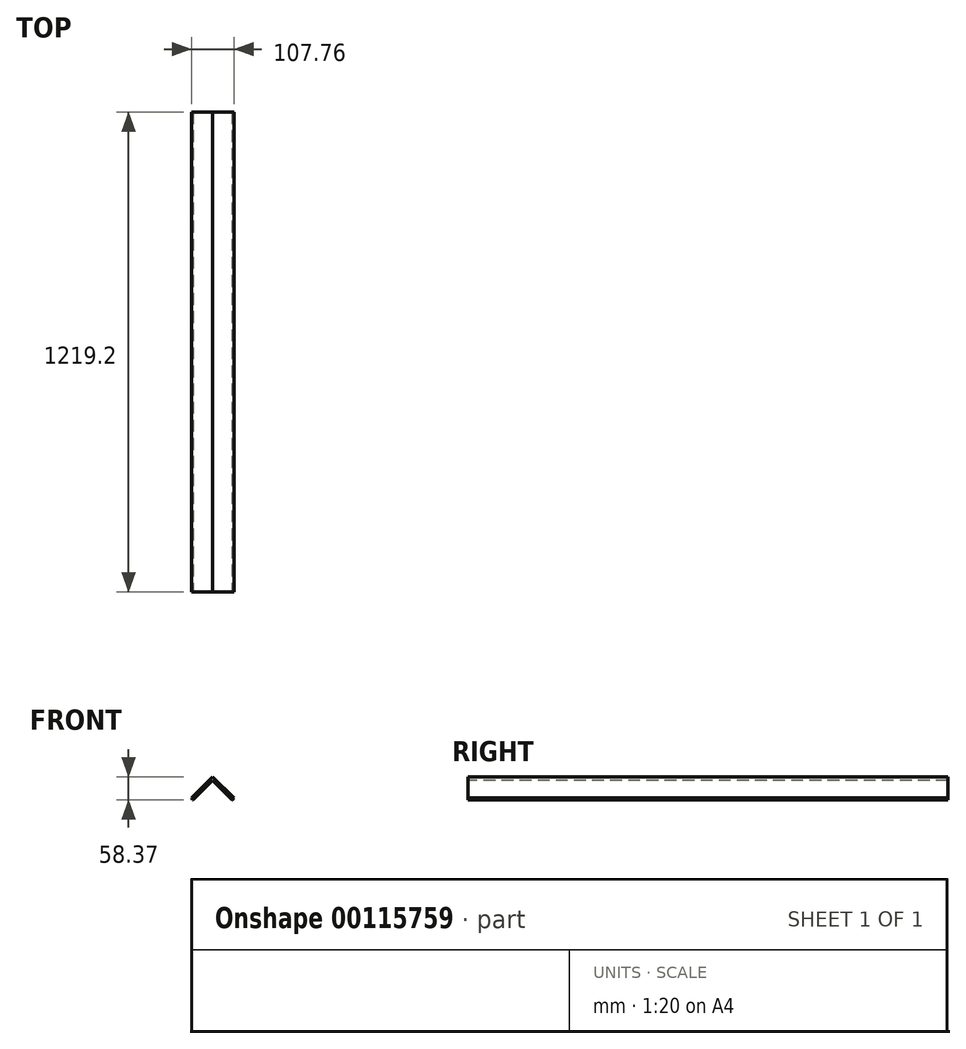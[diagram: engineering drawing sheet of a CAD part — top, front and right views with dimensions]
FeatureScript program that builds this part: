
annotation { "Feature Type Name" : "Feature", "Feature Type Description" : "" }
export const myFeature = defineFeature(function(context is Context, id is Id, definition is map)
    precondition{}
    {
        {
            var Q0;
            Q0=qCreatedBy(makeId("Front.planeOp"),FACE);
            var sketch = newSketch(context, id + "F0", { "sketchPlane" : qUnion([Q0])});
            skLineSegment(sketch, "E0", {"start": v(0, 0) * mm, "end": v(53.88, 53.88) * mm});
            skLineSegment(sketch, "E1", {"start": v(53.88, 53.88) * mm, "end": v(107.76, 0) * mm});
            skLineSegment(sketch, "E2.0", {"start": v(53.88, 44.9) * mm, "end": v(103.27, -4.5) * mm});
            skLineSegment(sketch, "E2.1", {"start": v(4.5, -4.5) * mm, "end": v(53.88, 44.9) * mm});
            skLineSegment(sketch, "E3", {"start": v(4.5, -4.5) * mm, "end": v(2.9, -4.5) * mm});
            skLineSegment(sketch, "E4", {"start": v(103.27, -4.5) * mm, "end": v(104.86, -4.5) * mm});
            skLineSegment(sketch, "E5", {"start": v(104.86, -4.5) * mm, "end": v(107.76, 0) * mm});
            skLineSegment(sketch, "E6", {"start": v(2.9, -4.5) * mm, "end": v(0, 0) * mm});
            skSolve(sketch);
        }
        {
            var Q0;
            Q0 = qSketchRegion(id + "F0", true);
            extrude(context, id + "F1", {"entities" : qUnion([Q0]), "oppositeDirection" : true, "depth" : 1219.2 * mm});
        }
    });
